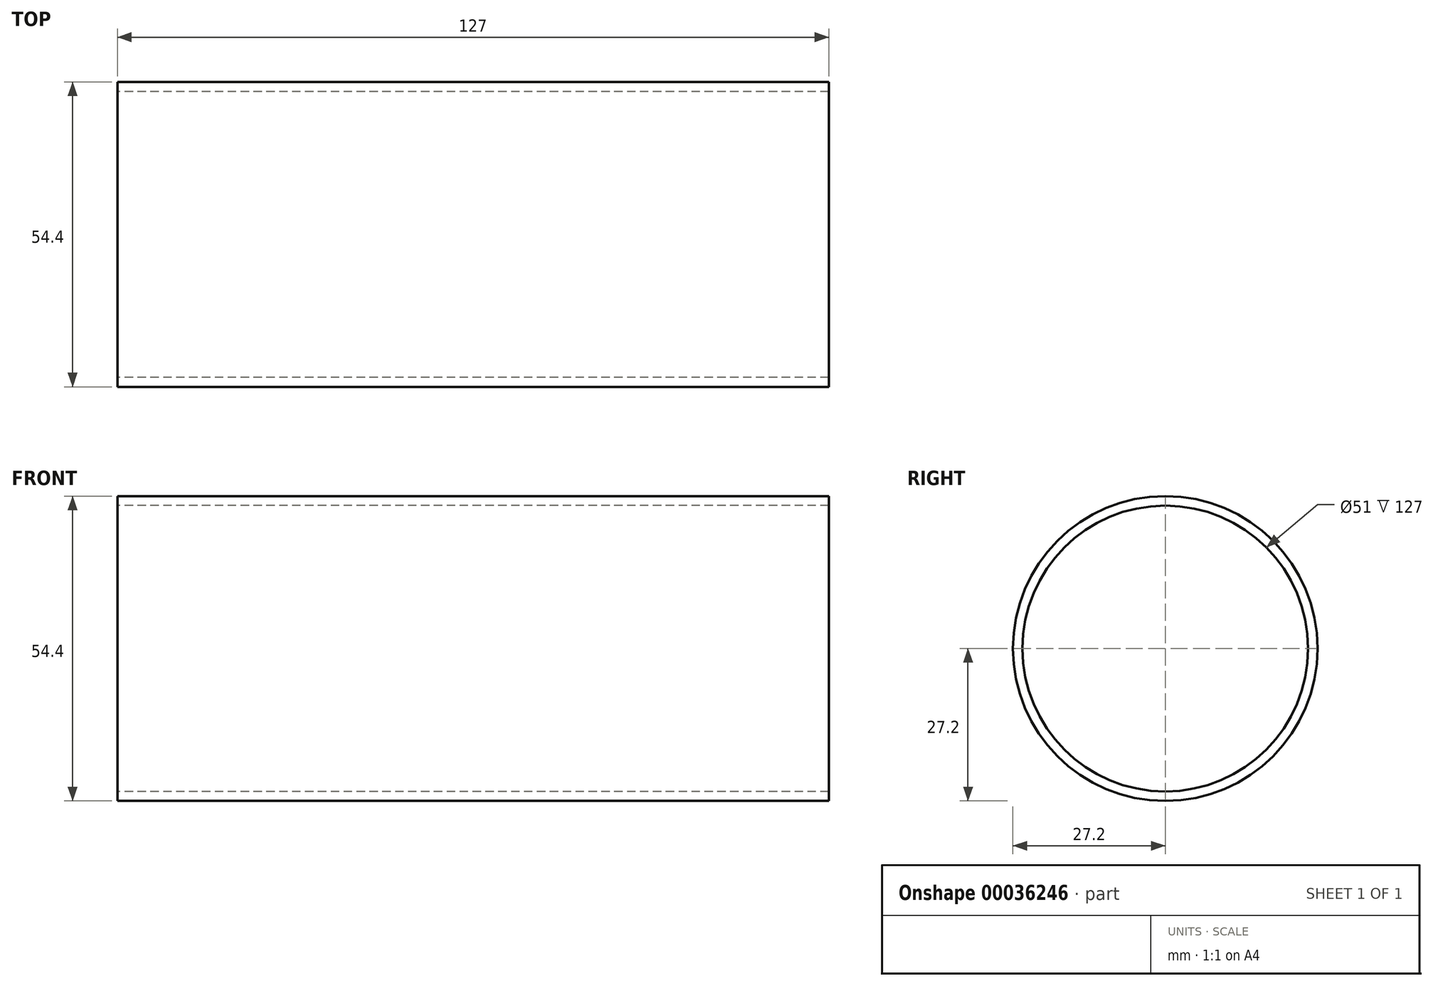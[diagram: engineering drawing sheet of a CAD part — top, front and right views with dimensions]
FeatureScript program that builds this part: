
annotation { "Feature Type Name" : "Feature", "Feature Type Description" : "" }
export const myFeature = defineFeature(function(context is Context, id is Id, definition is map)
    precondition{}
    {
        {
            var Q0;
            Q0=qCreatedBy(makeId("Right.planeOp"),FACE);
            var sketch = newSketch(context, id + "F0", { "sketchPlane" : qUnion([Q0])});
            skCircle(sketch, "E0", {"center": v(0, 0) * mm, "radius": 27.2 * mm});
            skCircle(sketch, "E1", {"center": v(0, 0) * mm, "radius": 25.5 * mm});
            skSolve(sketch);
        }
        {
            var Q0;
            Q0 = qSketchRegion(id + "F0", true);
            extrude(context, id + "F1", {"entities" : qUnion([Q0]), "endBound" : BoundingType.SYMMETRIC, "depth" : 127 * mm});
        }
    });
